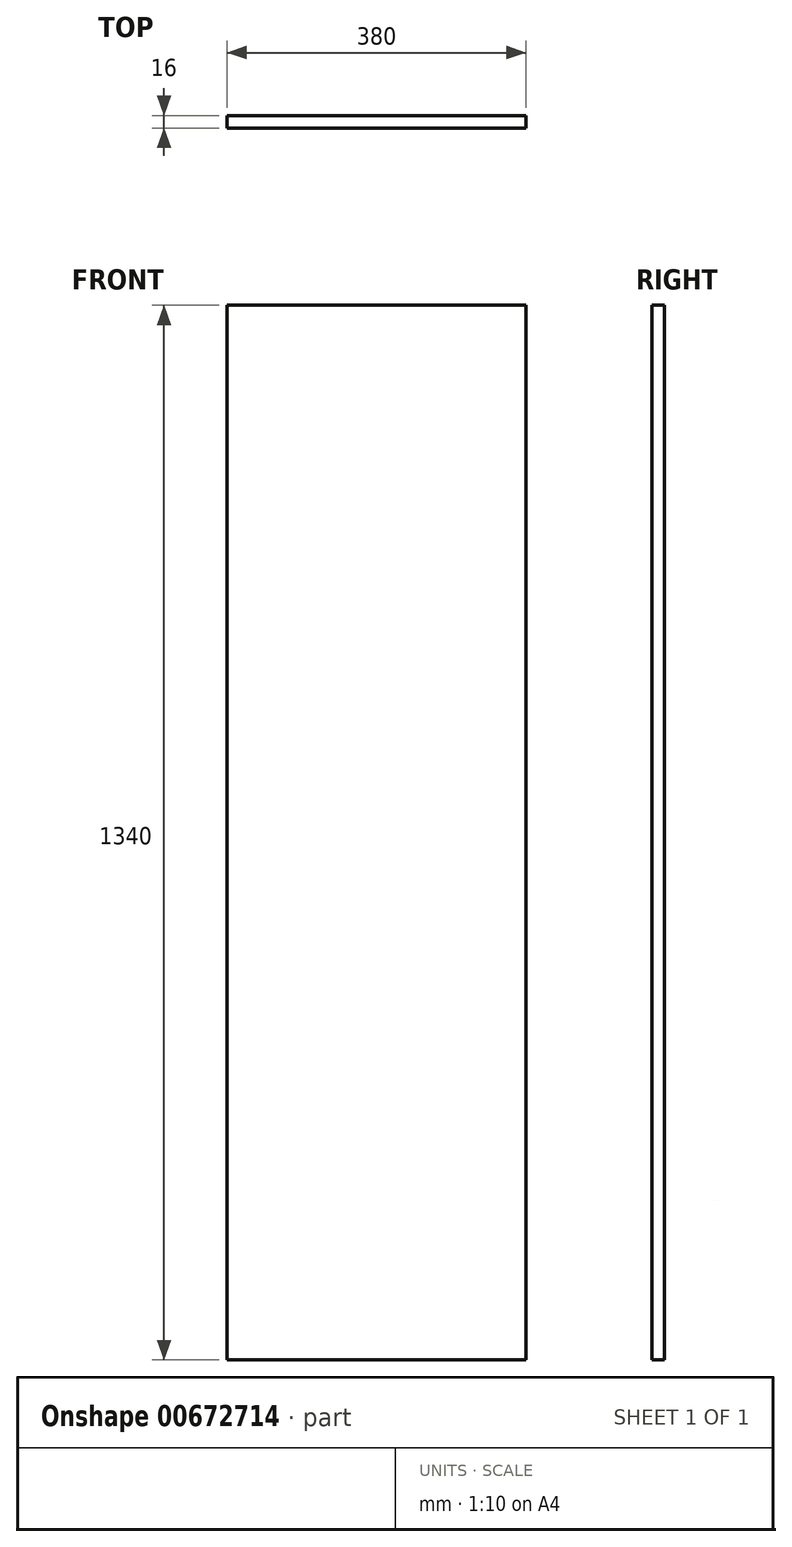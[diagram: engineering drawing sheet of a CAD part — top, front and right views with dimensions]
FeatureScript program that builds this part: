
annotation { "Feature Type Name" : "Feature", "Feature Type Description" : "" }
export const myFeature = defineFeature(function(context is Context, id is Id, definition is map)
    precondition{}
    {
        {
            var Q0;
            Q0=qCreatedBy(makeId("Front.planeOp"),FACE);
            var sketch = newSketch(context, id + "F0", { "sketchPlane" : qUnion([Q0])});
            skLineSegment(sketch, "E0.bottom", {"start": v(0, 0) * mm, "end": v(-380, 0) * mm});
            skLineSegment(sketch, "E0.top", {"start": v(0, 1340) * mm, "end": v(-380, 1340) * mm});
            skLineSegment(sketch, "E0.left", {"start": v(0, 0) * mm, "end": v(0, 1340) * mm});
            skLineSegment(sketch, "E0.right", {"start": v(-380, 0) * mm, "end": v(-380, 1340) * mm});
            skSolve(sketch);
        }
        {
            var Q0;
            Q0=makeQuery(id+"F0.imprint","IMPRINT",FACE,{"disambiguationData":[TD([[makeQuery(id+"F0.imprint","IMPRINT",EDGE,{"derivedFrom":sQuery(id+"F0.wireOp",EDGE,"E0.bottom")}),-1.0]])]});
            extrude(context, id + "F1", {"entities" : qUnion([Q0]), "depth" : 16 * mm, "offsetDistance" : 25 * mm});
        }
    });
